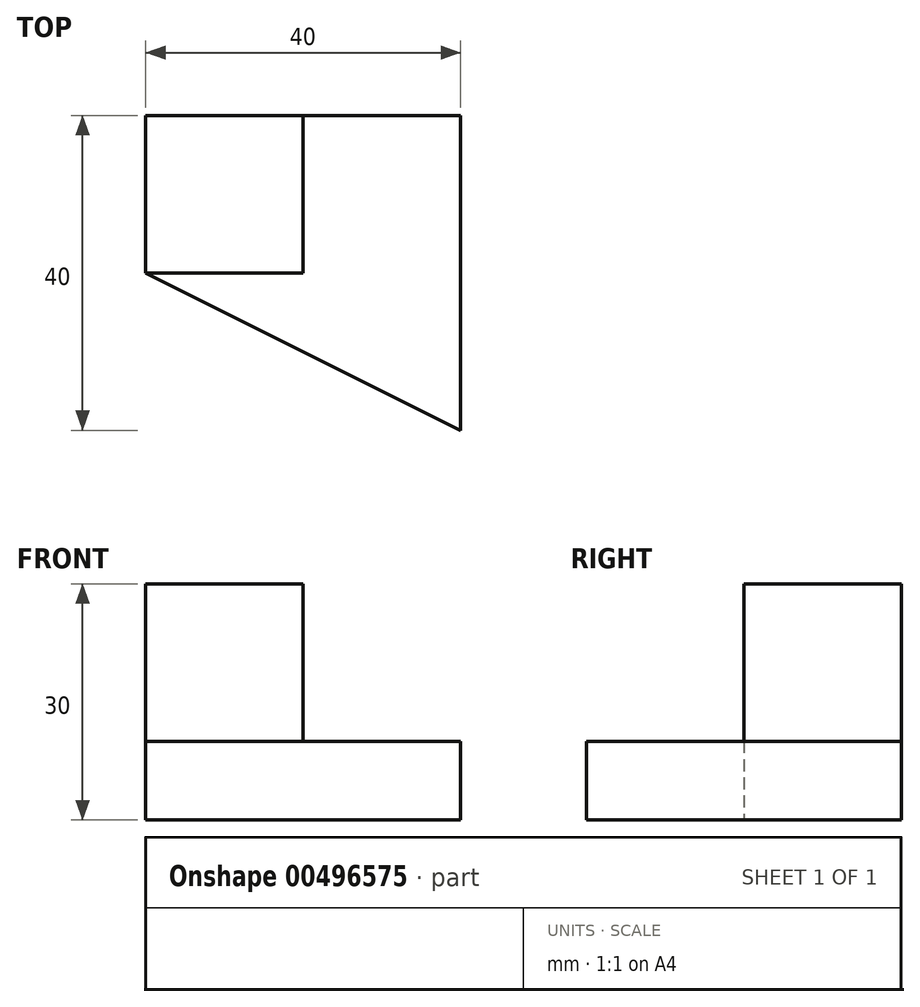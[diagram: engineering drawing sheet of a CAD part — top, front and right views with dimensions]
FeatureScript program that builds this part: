
annotation { "Feature Type Name" : "Feature", "Feature Type Description" : "" }
export const myFeature = defineFeature(function(context is Context, id is Id, definition is map)
    precondition{}
    {
        {
            var Q0;
            Q0=qCreatedBy(makeId("Top.planeOp"),FACE);
            var sketch = newSketch(context, id + "F0", { "sketchPlane" : qUnion([Q0])});
            skLineSegment(sketch, "E0", {"start": v(0, 0) * mm, "end": v(0, 20) * mm});
            skLineSegment(sketch, "E1", {"start": v(0, 20) * mm, "end": v(40, 20) * mm});
            skLineSegment(sketch, "E2", {"start": v(40, 20) * mm, "end": v(40, -20) * mm});
            skLineSegment(sketch, "E3", {"start": v(40, -20) * mm, "end": v(0, 0) * mm});
            skSolve(sketch);
        }
        {
            var Q0;
            Q0=makeQuery(id+"F0.imprint","IMPRINT",FACE,{"disambiguationData":[TD([[makeQuery(id+"F0.imprint","IMPRINT",EDGE,{"derivedFrom":sQuery(id+"F0.wireOp",EDGE,"E0")}),-1.0]])]});
            extrude(context, id + "F1", {"entities" : qUnion([Q0]), "depth" : 10 * mm});
        }
        {
            var Q0;
            Q0=makeQuery(id+"F1.opExtrude","CAP_FACE",FACE,{"disambiguationData":[OSD([sQuery(id+"F0.wireOp",EDGE,"E0"),sQuery(id+"F0.wireOp",EDGE,"E1"),sQuery(id+"F0.wireOp",EDGE,"E2"),sQuery(id+"F0.wireOp",EDGE,"E3")])],"isStart":false});
            var sketch = newSketch(context, id + "F2", { "sketchPlane" : qUnion([Q0])});
            skLineSegment(sketch, "E4.bottom", {"start": v(0, 0) * mm, "end": v(20, 0) * mm});
            skLineSegment(sketch, "E4.top", {"start": v(0, 20) * mm, "end": v(20, 20) * mm});
            skLineSegment(sketch, "E4.left", {"start": v(0, 0) * mm, "end": v(0, 20) * mm});
            skLineSegment(sketch, "E4.right", {"start": v(20, 0) * mm, "end": v(20, 20) * mm});
            skSolve(sketch);
        }
        {
            var Q0;
            Q0 = qSketchRegion(id + "F2", true);
            extrude(context, id + "F3", {"entities" : qUnion([Q0]), "operationType" : NewBodyOperationType.ADD, "depth" : 20 * mm});
        }
    });
